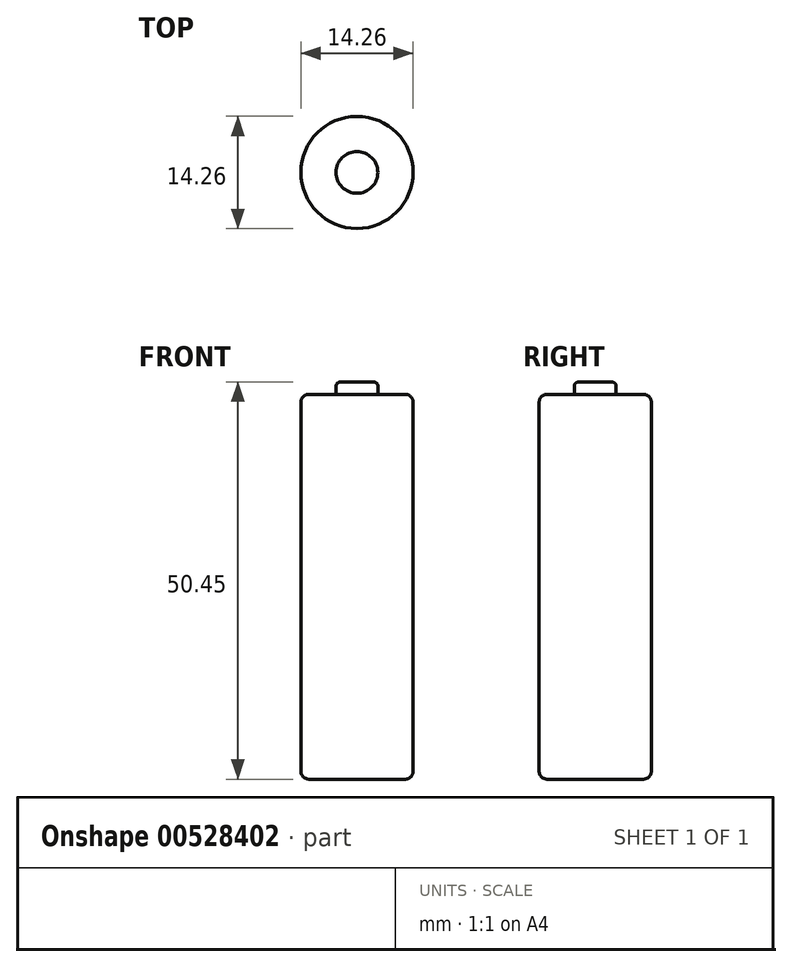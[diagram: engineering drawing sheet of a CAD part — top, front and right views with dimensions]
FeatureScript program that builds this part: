
annotation { "Feature Type Name" : "Feature", "Feature Type Description" : "" }
export const myFeature = defineFeature(function(context is Context, id is Id, definition is map)
    precondition{}
    {
        {
            var Q0;
            Q0=qCreatedBy(makeId("Top.planeOp"),FACE);
            var sketch = newSketch(context, id + "F0", { "sketchPlane" : qUnion([Q0])});
            skCircle(sketch, "E0", {"center": v(0, 0) * mm, "radius": 7.12 * mm});
            skSolve(sketch);
        }
        {
            var Q0;
            Q0 = qSketchRegion(id + "F0", true);
            extrude(context, id + "F1", {"entities" : qUnion([Q0]), "flatOperationType" : FlatOperationType.REMOVE, "endBound" : BoundingType.SYMMETRIC, "depth" : 48.9 * mm, "offsetDistance" : 25 * mm, "domain" : OperationDomain.MODEL});
        }
        {
            var Q0;
            Q0=makeQuery(id+"F1.opExtrude","CAP_FACE",FACE,{"disambiguationData":[OSD([sQuery(id+"F0.wireOp",EDGE,"E0")])],"isStart":false});
            var sketch = newSketch(context, id + "F2", { "sketchPlane" : qUnion([Q0])});
            skCircle(sketch, "E1", {"center": v(0, 0) * mm, "radius": 2.65 * mm});
            skSolve(sketch);
        }
        {
            var Q0;
            Q0 = qSketchRegion(id + "F2", true);
            extrude(context, id + "F3", {"entities" : qUnion([Q0]), "operationType" : NewBodyOperationType.ADD, "depth" : 1.55 * mm, "offsetDistance" : 25 * mm});
        }
        {
            var Q0;
            Q0=makeQuery(id+"F3.opExtrude","CAP_EDGE",EDGE,{"disambiguationData":[OSD([sQuery(id+"F2.wireOp",EDGE,"E1")])],"isStart":false});
            fillet(context, id + "F4", {"entities" : qUnion([Q0]), "radius" : .5 * mm, "tangentPropagation" : true, "allowEdgeOverflow" : false});
        }
        {
            var Q0;
            Q0=makeQuery(id+"F1.opExtrude","CAP_EDGE",EDGE,{"disambiguationData":[OSD([sQuery(id+"F0.wireOp",EDGE,"E0")])],"isStart":false});
            var Q1;
            Q1=makeQuery(id+"F1.opExtrude","CAP_EDGE",EDGE,{"disambiguationData":[OSD([sQuery(id+"F0.wireOp",EDGE,"E0")])],"isStart":true});
            fillet(context, id + "F5", {"entities" : qUnion([Q0, Q1]), "radius" : 1 * mm, "tangentPropagation" : true, "allowEdgeOverflow" : false});
        }
    });
